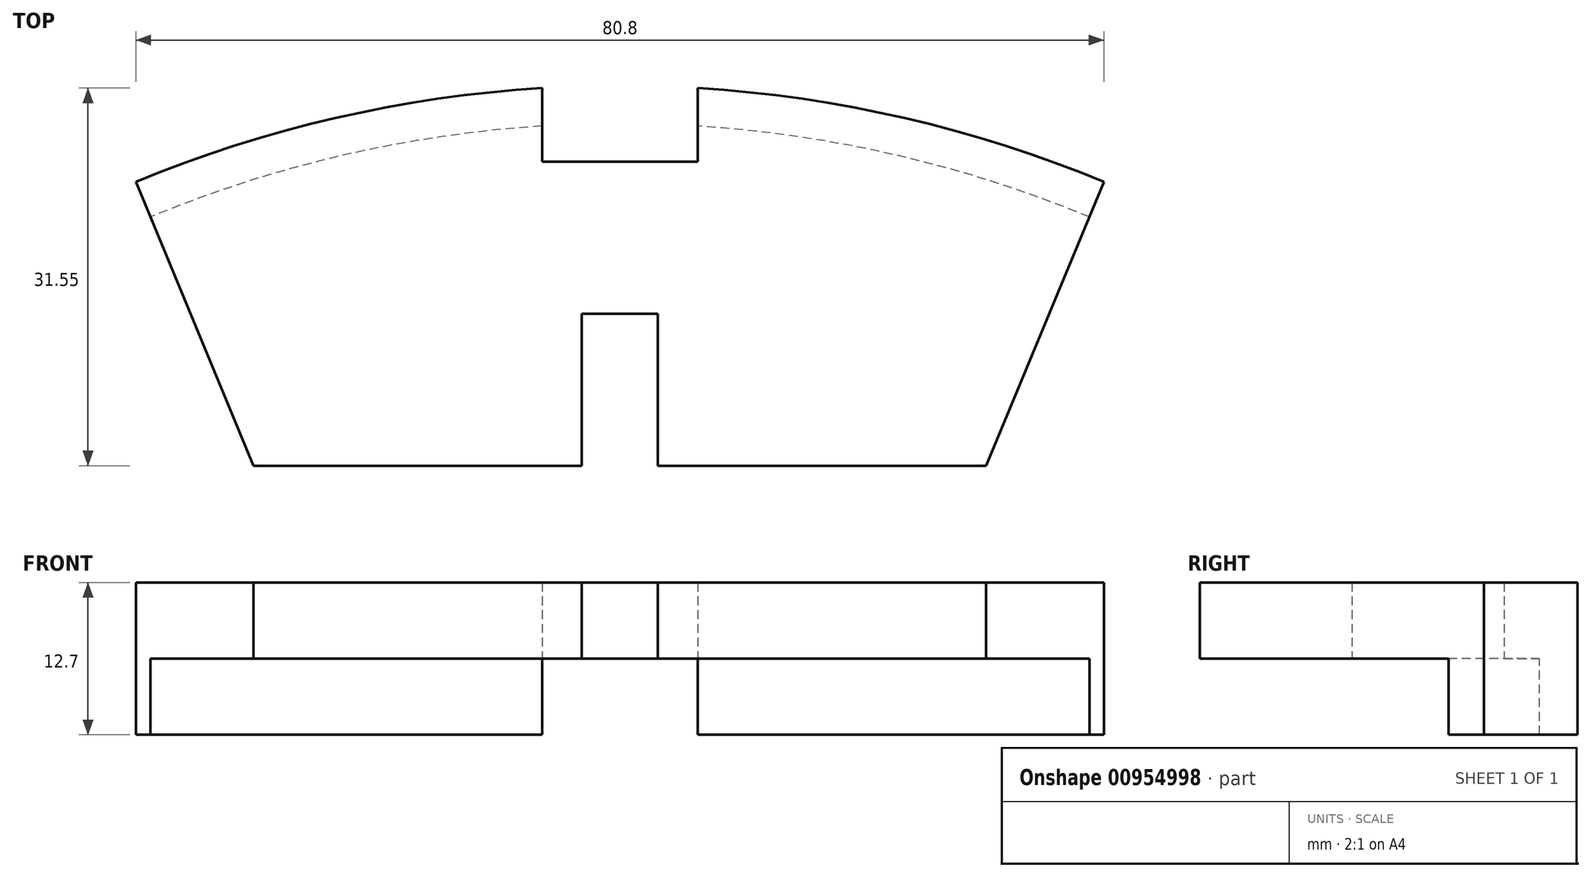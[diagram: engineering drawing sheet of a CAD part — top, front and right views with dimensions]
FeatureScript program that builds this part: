
annotation { "Feature Type Name" : "Feature", "Feature Type Description" : "" }
export const myFeature = defineFeature(function(context is Context, id is Id, definition is map)
    precondition{}
    {
        {
            var Q0;
            Q0=qCreatedBy(makeId("Top.planeOp"),FACE);
            var sketch = newSketch(context, id + "F0", { "sketchPlane" : qUnion([Q0])});
            skCircle(sketch, "E0", {"center": v(0, 0) * mm, "radius": 102.4 * mm, "construction": true});
            skCircle(sketch, "E1", {"center": v(0, 0) * mm, "radius": 99.22 * mm, "construction": true});
            skLineSegment(sketch, "E2", {"start": v(0, 0) * mm, "end": v(-40.4, 97.53) * mm, "construction": true});
            skLineSegment(sketch, "E3", {"start": v(0, 0) * mm, "end": v(40.4, 97.53) * mm, "construction": true});
            skArc(sketch, "E4", {"start": v(40.4, 97.53) * mm, "mid": v(0, 105.57) * mm, "end": v(-40.4, 97.53) * mm});
            skLineSegment(sketch, "E5", {"start": v(-40.4, 97.53) * mm, "end": v(-30.58, 73.82) * mm});
            skLineSegment(sketch, "E6", {"start": v(-30.58, 73.82) * mm, "end": v(30.58, 73.82) * mm});
            skLineSegment(sketch, "E7", {"start": v(30.58, 73.82) * mm, "end": v(40.4, 97.53) * mm});
            skSolve(sketch);
        }
        {
            var Q0;
            Q0 = qSketchRegion(id + "F0", true);
            extrude(context, id + "F1", {"entities" : qUnion([Q0]), "depth" : 6.35 * mm, "offsetDistance" : 25.4 * mm});
        }
        {
            var Q0;
            Q0=qCreatedBy(makeId("Right.planeOp"),FACE);
            var sketch = newSketch(context, id + "F2", { "sketchPlane" : qUnion([Q0])});
            skPoint(sketch, "E8.0", {"position": v(105.57, 0) * mm});
            skLineSegment(sketch, "E9", {"start": v(105.57, 0) * mm, "end": v(105.57, -6.35) * mm});
            skLineSegment(sketch, "E10", {"start": v(105.57, -6.35) * mm, "end": v(102.4, -6.35) * mm});
            skLineSegment(sketch, "E11", {"start": v(102.4, -6.35) * mm, "end": v(102.4, 0) * mm});
            skLineSegment(sketch, "E12", {"start": v(102.4, 0) * mm, "end": v(105.57, 0) * mm});
            skSolve(sketch);
        }
        {
            var Q0;
            Q0=qCreatedBy(makeId("Front.planeOp"),FACE);
            var sketch = newSketch(context, id + "F3", { "sketchPlane" : qUnion([Q0])});
            skLineSegment(sketch, "E13", {"start": v(0, 76.75) * mm, "end": v(0, -63.42) * mm, "construction": true});
            skSolve(sketch);
        }
        {
            var Q0;
            Q0=makeQuery(id+"F2.imprint","IMPRINT",FACE,{"disambiguationData":[TD([[makeQuery(id+"F2.imprint","IMPRINT",EDGE,{"derivedFrom":sQuery(id+"F2.wireOp",EDGE,"E9")}),-1.0]])]});
            var Q1;
            Q1=sQuery(id+"F3.wireOp",EDGE,"E13");
            revolve(context, id + "F4", {"operationType" : NewBodyOperationType.ADD, "surfaceOperationType" : NewSurfaceOperationType.NEW, "entities" : qUnion([Q0]), "axis" : qUnion([Q1]), "revolveType" : RevolveType.SYMMETRIC, "angle" : 45 * degree});
        }
        {
            var Q0;
            Q0=makeQuery(id+"F1.opExtrude","CAP_FACE",FACE,{"disambiguationData":[OSD([sQuery(id+"F0.wireOp",EDGE,"E4"),sQuery(id+"F0.wireOp",EDGE,"E5"),sQuery(id+"F0.wireOp",EDGE,"E6"),sQuery(id+"F0.wireOp",EDGE,"E7")])],"isStart":true});
            var sketch = newSketch(context, id + "F5", { "sketchPlane" : qUnion([Q0])});
            skLineSegment(sketch, "E14.bottom", {"start": v(-3.18, -73.82) * mm, "end": v(3.17, -73.82) * mm});
            skLineSegment(sketch, "E14.top", {"start": v(-3.18, -86.52) * mm, "end": v(3.17, -86.52) * mm});
            skLineSegment(sketch, "E14.left", {"start": v(-3.18, -73.82) * mm, "end": v(-3.18, -86.52) * mm});
            skLineSegment(sketch, "E14.right", {"start": v(3.17, -73.82) * mm, "end": v(3.17, -86.52) * mm});
            skPoint(sketch, "E14.middle", {"position": v(0, -80.17) * mm});
            skLineSegment(sketch, "E15.bottom", {"start": v(6.5, -111.92) * mm, "end": v(-6.5, -111.92) * mm});
            skLineSegment(sketch, "E15.top", {"start": v(6.5, -99.22) * mm, "end": v(-6.5, -99.22) * mm});
            skLineSegment(sketch, "E15.left", {"start": v(6.5, -111.92) * mm, "end": v(6.5, -99.22) * mm});
            skLineSegment(sketch, "E15.right", {"start": v(-6.5, -111.92) * mm, "end": v(-6.5, -99.22) * mm});
            skPoint(sketch, "E15.middle", {"position": v(0, -105.57) * mm});
            skSolve(sketch);
        }
        {
            var Q0;
            Q0 = qSketchRegion(id + "F5", true);
            extrude(context, id + "F6", {"entities" : qUnion([Q0]), "operationType" : NewBodyOperationType.REMOVE, "oppositeDirection" : true, "depth" : 25.4 * mm, "offsetDistance" : 25.4 * mm, "symmetric" : true});
        }
    });
